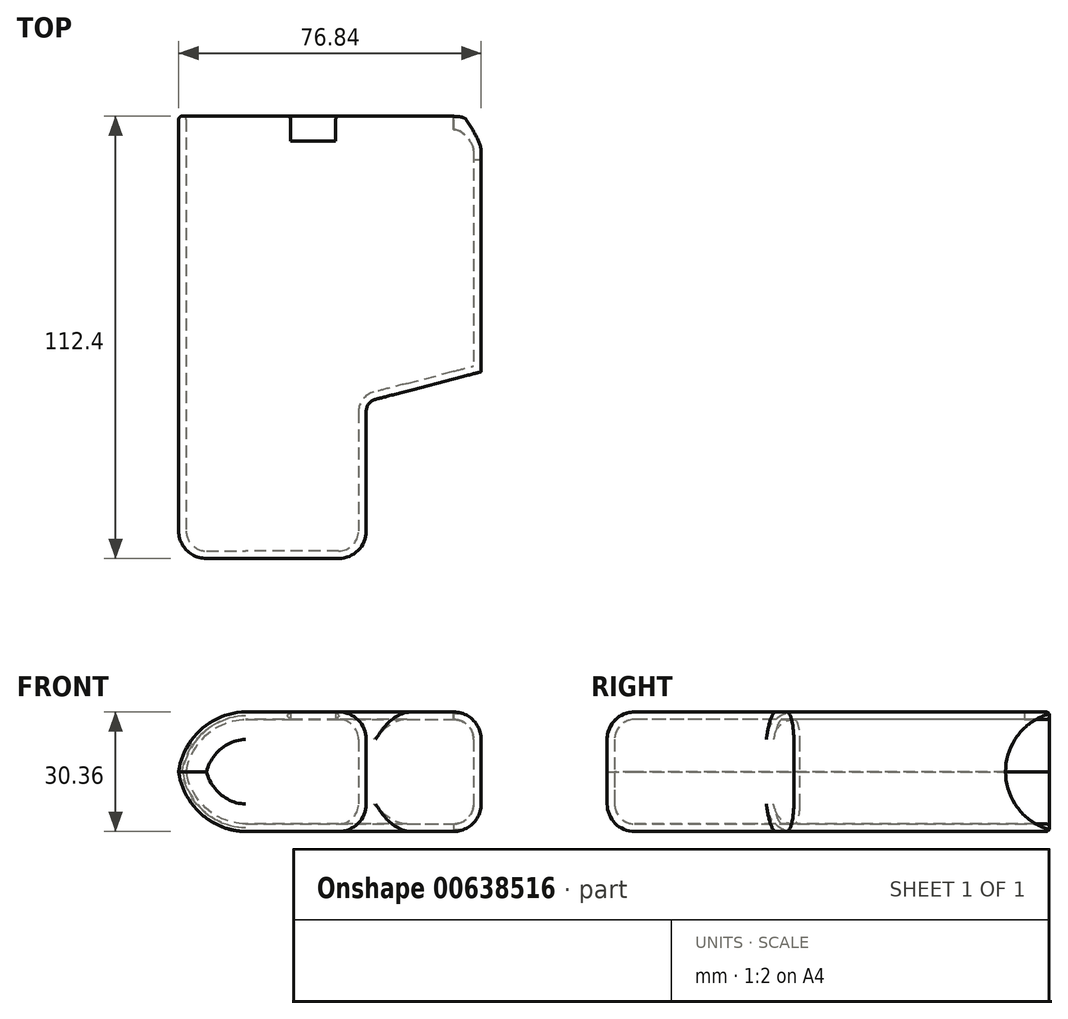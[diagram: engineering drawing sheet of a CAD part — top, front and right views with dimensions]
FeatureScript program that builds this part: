
annotation { "Feature Type Name" : "Feature", "Feature Type Description" : "" }
export const myFeature = defineFeature(function(context is Context, id is Id, definition is map)
    precondition{}
    {
        {
            var Q0;
            Q0=qCreatedBy(makeId("Top.planeOp"),FACE);
            var sketch = newSketch(context, id + "F0", { "sketchPlane" : qUnion([Q0])});
            skLineSegment(sketch, "E0", {"start": v(-37.72, -82.37) * mm, "end": v(-37.72, 28.12) * mm});
            skLineSegment(sketch, "E1", {"start": v(35.43, 28.12) * mm, "end": v(35.43, -35.38) * mm});
            skLineSegment(sketch, "E2", {"start": v(6.22, -43) * mm, "end": v(6.22, -82.37) * mm});
            skLineSegment(sketch, "E3", {"start": v(6.22, -82.37) * mm, "end": v(-37.72, -82.37) * mm});
            skLineSegment(sketch, "E4", {"start": v(-37.72, 28.12) * mm, "end": v(35.43, 28.12) * mm});
            skLineSegment(sketch, "E5", {"start": v(6.22, -43) * mm, "end": v(35.43, -35.38) * mm});
            skSolve(sketch);
        }
        {
            var Q0;
            Q0=makeQuery(id+"F0.imprint","IMPRINT",FACE,{"disambiguationData":[TD([[makeQuery(id+"F0.imprint","IMPRINT",EDGE,{"derivedFrom":sQuery(id+"F0.wireOp",EDGE,"E0")}),-1.0]])]});
            extrude(context, id + "F1", {"entities" : qUnion([Q0]), "endBound" : BoundingType.SYMMETRIC, "depth" : 26.54 * mm, "offsetDistance" : 25.4 * mm});
        }
        {
            var Q0;
            Q0=makeQuery(id+"F1.opExtrude","CAP_EDGE",EDGE,{"disambiguationData":[OSD([sQuery(id+"F0.wireOp",EDGE,"E0")])],"isStart":false});
            var Q1;
            Q1=makeQuery(id+"F1.opExtrude","CAP_EDGE",EDGE,{"disambiguationData":[OSD([sQuery(id+"F0.wireOp",EDGE,"E0")])],"isStart":true});
            fillet(context, id + "F2", {"entities" : qUnion([Q0, Q1]), "radius" : 15.24 * mm, "tangentPropagation" : true, "rho" : .4, "crossSection" : FilletCrossSection.CONIC, "allowEdgeOverflow" : false});
        }
        {
            var Q0;
            Q0=makeQuery(id+"F1.opExtrude","SWEPT_FACE",FACE,{"disambiguationData":[OSD([sQuery(id+"F0.wireOp",EDGE,"E3")])]});
            var Q1;
            Q1=makeQuery(id+"F1.opExtrude","SWEPT_FACE",FACE,{"disambiguationData":[OSD([sQuery(id+"F0.wireOp",EDGE,"E2")])]});
            var Q2;
            Q2=makeQuery(id+"F1.opExtrude","CAP_EDGE",EDGE,{"disambiguationData":[OSD([sQuery(id+"F0.wireOp",EDGE,"E1")])],"isStart":true});
            var Q3;
            Q3=makeQuery(id+"F1.opExtrude","CAP_EDGE",EDGE,{"disambiguationData":[OSD([sQuery(id+"F0.wireOp",EDGE,"E1")])],"isStart":false});
            fillet(context, id + "F3", {"entities" : qUnion([Q0, Q1, Q2, Q3]), "radius" : 5.08 * mm, "tangentPropagation" : true, "allowEdgeOverflow" : false});
        }
        {
            var Q0;
            Q0=makeQuery(id+"F1.opExtrude","SWEPT_FACE",FACE,{"disambiguationData":[OSD([sQuery(id+"F0.wireOp",EDGE,"E4")])]});
            shell(context, id + "F4", {"entities" : qUnion([Q0]), "thickness" : 1.9 * mm, "oppositeDirection" : true});
        }
        {
            var Q0;
            Q0=qCreatedBy(makeId("Top.planeOp"),FACE);
            var sketch = newSketch(context, id + "F5", { "sketchPlane" : qUnion([Q0])});
            skPoint(sketch, "E6.visualSharp", {"position": v(3.48, 27.22) * mm});
            skLineSegment(sketch, "E7", {"start": v(0.38, -82.37) * mm, "end": v(0.38, 21.77) * mm, "construction": true});
            skLineSegment(sketch, "E8", {"start": v(0.38, 21.77) * mm, "end": v(-37.72, 21.77) * mm, "construction": true});
            skLineSegment(sketch, "E9.bottom", {"start": v(0.38, 37.51) * mm, "end": v(-11.05, 37.51) * mm});
            skLineSegment(sketch, "E9.top", {"start": v(0.38, 21.77) * mm, "end": v(-11.05, 21.77) * mm});
            skLineSegment(sketch, "E9.left", {"start": v(0.38, 37.51) * mm, "end": v(0.38, 21.77) * mm});
            skLineSegment(sketch, "E9.right", {"start": v(-11.05, 37.51) * mm, "end": v(-11.05, 21.77) * mm});
            skSolve(sketch);
        }
        {
            var Q0;
            Q0 = qSketchRegion(id + "F5", true);
            extrude(context, id + "F6", {"entities" : qUnion([Q0]), "operationType" : NewBodyOperationType.REMOVE, "depth" : 25.4 * mm, "offsetDistance" : 25.4 * mm});
        }
        {
            var Q0;
            {var subQ5=sQuery(id+"F0.wireOp",EDGE,"E4");var subQ13=makeQuery(id+"F1.opExtrude","SWEPT_FACE",FACE,{"disambiguationData":[OSD([subQ5])]});Q0=makeQuery(id+"F6.boolean.opBoolean","SPLIT",FACE,{"disambiguationData":[TD([makeQuery(id+"F6.opExtrude","SWEPT_FACE",FACE,{"disambiguationData":[OSD([sQuery(id+"F5.wireOp",EDGE,"E9.right")])]})])],"derivedFrom":subQ13});}
            var Q1;
            {var subQ0=sQuery(id+"F0.wireOp",EDGE,"E4");var subQ10=makeQuery(id+"F1.opExtrude","SWEPT_FACE",FACE,{"disambiguationData":[OSD([subQ0])]});Q1=makeQuery(id+"F6.boolean.opBoolean","SPLIT",FACE,{"disambiguationData":[TD([makeQuery(id+"F6.opExtrude","SWEPT_FACE",FACE,{"disambiguationData":[OSD([sQuery(id+"F5.wireOp",EDGE,"E9.left")])]})])],"derivedFrom":subQ10});}
            fillet(context, id + "F7", {"entities" : qUnion([Q0, Q1]), "radius" : 0.89 * mm, "tangentPropagation" : true, "allowEdgeOverflow" : false});
        }
        {
            var Q0;
            Q0=qCreatedBy(makeId("Front.planeOp"),FACE);
            var sketch = newSketch(context, id + "F8", { "sketchPlane" : qUnion([Q0])});
            skLineSegment(sketch, "E10.bottom", {"start": v(-43.08, -19.25) * mm, "end": v(42.92, -19.25) * mm});
            skLineSegment(sketch, "E10.top", {"start": v(-43.08, 0) * mm, "end": v(42.92, 0) * mm});
            skLineSegment(sketch, "E10.left", {"start": v(-43.08, -19.25) * mm, "end": v(-43.08, 0) * mm});
            skLineSegment(sketch, "E10.right", {"start": v(42.92, -19.25) * mm, "end": v(42.92, 0) * mm});
            skSolve(sketch);
        }
        {
            var Q0;
            Q0=qCreatedBy(makeId("Right.planeOp"),FACE);
            var sketch = newSketch(context, id + "F9", { "sketchPlane" : qUnion([Q0])});
            skCircle(sketch, "E11", {"center": v(32.18, 0) * mm, "radius": 15.24 * mm});
            skSolve(sketch);
        }
        {
            var Q0;
            Q0=makeQuery(id+"F9.imprint","IMPRINT",FACE,{"disambiguationData":[TD([[makeQuery(id+"F9.imprint","IMPRINT",EDGE,{"derivedFrom":sQuery(id+"F9.wireOp",EDGE,"E11")}),1.0]])]});
            extrude(context, id + "F10", {"entities" : qUnion([Q0]), "operationType" : NewBodyOperationType.REMOVE, "depth" : 50.8 * mm, "offsetDistance" : 25.4 * mm, "hasSecondDirection" : true, "secondDirectionOppositeDirection" : false, "secondDirectionDepth" : 30.35 * mm});
        }
    });
